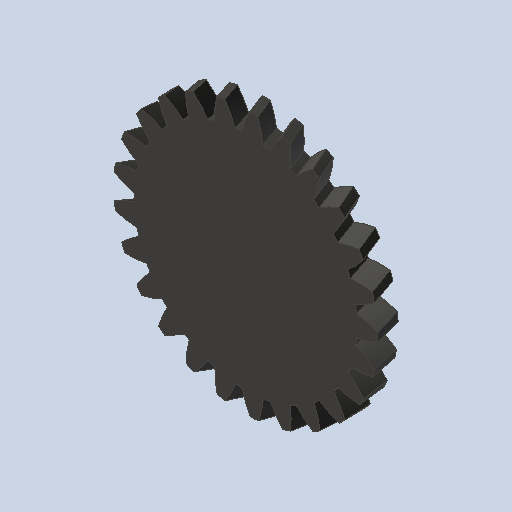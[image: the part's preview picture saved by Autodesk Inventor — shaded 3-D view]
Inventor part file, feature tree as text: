
AUTODESK INVENTOR PART (.ipt)
format: ipt  version: 2023 (Build 270158000, 158)  size: 434,688 bytes
history: native  units: mm (DEFAULTED — no unit token found)
features: plane x3, other x3, sketch x2, extrude x1
ambient origin geometry x8: Origin, YZ Plane, XZ Plane, XY Plane, X Axis, Y Axis, Z Axis, Center Point
bodies: Solid1 (feature_tree)
feature tree (9):
  extrude  "Extrusion1"  Depth=10.0mm TaperAngle=0.0deg
  plane  "Work Plane2"
  plane  "Work Plane8"
  plane  "Work Plane9"
  other  "Spur Gear"
  sketch  "Sketch1"  dims[d0=128.719999mm d1=10.0mm d2=0.0mm]
  sketch  "Sketch2"  dims[d3=119.719999mm d4=10.0mm d5=0.0mm d16=107.95mm d17=0.0mm d34=1.256637mm d39=0.0mm d41=0.0mm d43=107.95mm d46=107.95mm d47=0.0mm d48=0.0mm]
  other  "Srf1"
  other  "Pitch Diameter"
